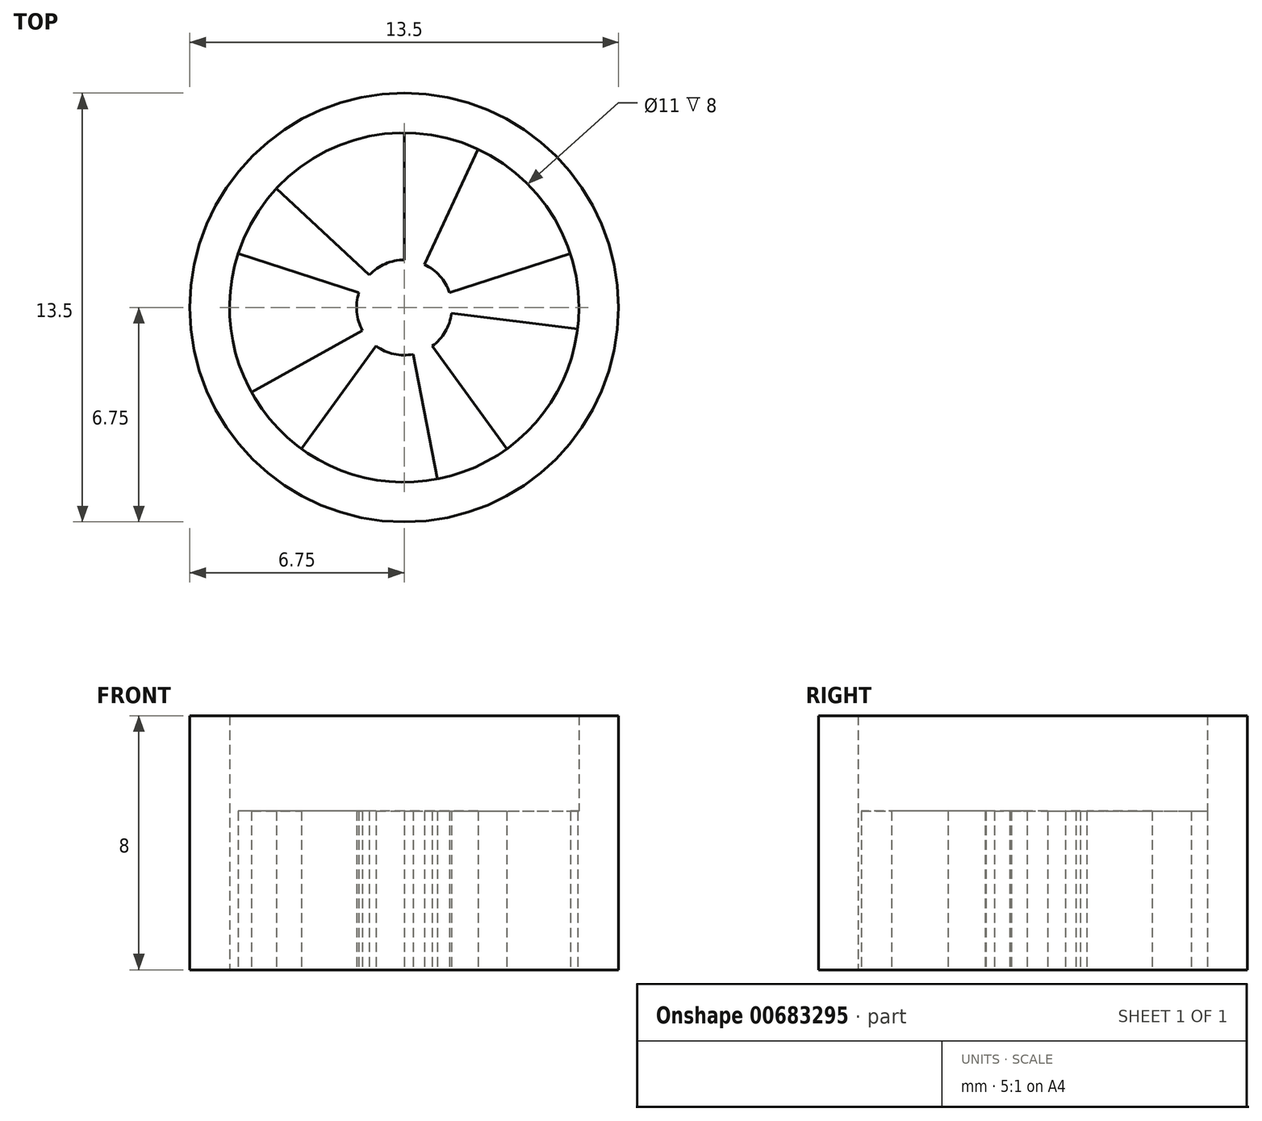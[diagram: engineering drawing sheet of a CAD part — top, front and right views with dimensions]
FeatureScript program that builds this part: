
annotation { "Feature Type Name" : "Feature", "Feature Type Description" : "" }
export const myFeature = defineFeature(function(context is Context, id is Id, definition is map)
    precondition{}
    {
        {
            var Q0;
            Q0=qCreatedBy(makeId("Top.planeOp"),FACE);
            var sketch = newSketch(context, id + "F0", { "sketchPlane" : qUnion([Q0])});
            skCircle(sketch, "E0", {"center": v(0, 0) * mm, "radius": 6.75 * mm});
            skCircle(sketch, "E1", {"center": v(0, 0) * mm, "radius": 5.5 * mm});
            skCircle(sketch, "E2", {"center": v(0, 0) * mm, "radius": 1.5 * mm});
            skLineSegment(sketch, "E3", {"start": v(0, 1.5) * mm, "end": v(0, 5.5) * mm});
            skLineSegment(sketch, "E4", {"start": v(0.63, 1.36) * mm, "end": v(2.32, 4.98) * mm});
            skLineSegment(sketch, "E5.1.0", {"start": v(-1.43, 0.46) * mm, "end": v(-5.23, 1.7) * mm});
            skLineSegment(sketch, "E5.1.1", {"start": v(-1.1, 1.02) * mm, "end": v(-4.02, 3.75) * mm});
            skLineSegment(sketch, "E5.2.0", {"start": v(-0.88, -1.21) * mm, "end": v(-3.23, -4.45) * mm});
            skLineSegment(sketch, "E5.2.1", {"start": v(-1.31, -0.73) * mm, "end": v(-4.81, -2.67) * mm});
            skLineSegment(sketch, "E5.3.0", {"start": v(0.88, -1.21) * mm, "end": v(3.23, -4.45) * mm});
            skLineSegment(sketch, "E5.3.1", {"start": v(0.29, -1.47) * mm, "end": v(1.05, -5.4) * mm});
            skLineSegment(sketch, "E5.4.0", {"start": v(1.43, 0.46) * mm, "end": v(5.23, 1.7) * mm});
            skLineSegment(sketch, "E5.4.1", {"start": v(1.49, -0.18) * mm, "end": v(5.46, -0.67) * mm});
            skSolve(sketch);
        }
        {
            var Q0;
            Q0 = qSketchRegion(id + "F0", true);
            extrude(context, id + "F1", {"entities" : qUnion([Q0]), "depth" : 8 * mm, "offsetDistance" : 25 * mm});
        }
        {
            var Q0;
            Q0 = qSketchRegion(id + "F0", true);
            var Q1;
            {var subQ0=sQuery(id+"F0.wireOp",EDGE,"E3");Q1=makeQuery(id+"F0.imprint","IMPRINT",FACE,{"disambiguationData":[TD([[makeQuery(id+"F0.imprint","IMPRINT",EDGE,{"derivedFrom":subQ0}),-1.0]])]});}
            var Q2;
            {var subQ0=sQuery(id+"F0.wireOp",EDGE,"E5.1.0");Q2=makeQuery(id+"F0.imprint","IMPRINT",FACE,{"disambiguationData":[TD([[makeQuery(id+"F0.imprint","IMPRINT",EDGE,{"derivedFrom":subQ0}),-1.0]])]});}
            var Q3;
            {var subQ0=sQuery(id+"F0.wireOp",EDGE,"E5.2.0");Q3=makeQuery(id+"F0.imprint","IMPRINT",FACE,{"disambiguationData":[TD([[makeQuery(id+"F0.imprint","IMPRINT",EDGE,{"derivedFrom":subQ0}),-1.0]])]});}
            var Q4;
            {var subQ0=sQuery(id+"F0.wireOp",EDGE,"E5.3.0");Q4=makeQuery(id+"F0.imprint","IMPRINT",FACE,{"disambiguationData":[TD([[makeQuery(id+"F0.imprint","IMPRINT",EDGE,{"derivedFrom":subQ0}),-1.0]])]});}
            var Q5;
            {var subQ0=sQuery(id+"F0.wireOp",EDGE,"E5.4.0");Q5=makeQuery(id+"F0.imprint","IMPRINT",FACE,{"disambiguationData":[TD([[makeQuery(id+"F0.imprint","IMPRINT",EDGE,{"derivedFrom":subQ0}),-1.0]])]});}
            var Q6;
            {var subQ0=sQuery(id+"F0.wireOp",EDGE,"E2");var subQ4=makeQuery(id+"F0.imprint","INTERSECT",VERTEX,{"derivedFrom":[subQ0,sQuery(id+"F0.wireOp",EDGE,"E4")]});Q6=makeQuery(id+"F0.imprint","IMPRINT",FACE,{"disambiguationData":[TD([[makeQuery(id+"F0.imprint","IMPRINT",EDGE,{"disambiguationData":[TD([[subQ4,1.0]])],"derivedFrom":subQ0}),1.0]])]});}
            extrude(context, id + "F2", {"entities" : qUnion([Q0, Q1, Q2, Q3, Q4, Q5, Q6]), "operationType" : NewBodyOperationType.ADD, "depth" : 5 * mm, "offsetDistance" : 25 * mm});
        }
    });
